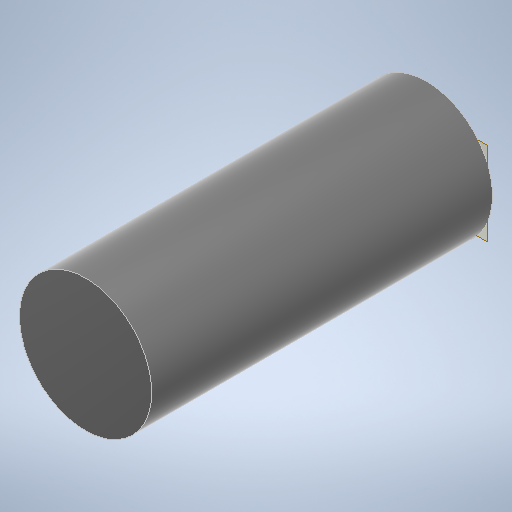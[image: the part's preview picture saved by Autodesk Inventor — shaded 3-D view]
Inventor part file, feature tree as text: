
AUTODESK INVENTOR PART (.ipt)
format: ipt  version: 2025.1 (Build 291241020, 241B)  size: 427,520 bytes
history: native  units: mm
features: extrude x8, sketch x8, plane x1, mirror x1
ambient origin geometry x8: Origin, YZ Plane, XZ Plane, XY Plane, X Axis, Y Axis, Z Axis, Center Point
bodies: Solid1 (feature_tree)
feature tree (18):
  extrude  "Extrusion1"  Depth=39.0mm
  plane  "Work Plane1"
  extrude  "Extrusion2"  Depth=3.0mm TaperAngle=0.0deg
  mirror  "Mirror1"
  extrude  "Extrusion5"  Depth=10.0mm TaperAngle=0.0deg
  extrude  "Extrusion6"  Depth=7.0mm
  extrude  "Extrusion7"  Depth=20.4mm
  extrude  "Extrusion8"  TaperAngle=0.0deg  [1 undecoded]
  extrude  "Extrusion9"  Depth=0.9mm
  extrude  "Extrusion10"  [1 undecoded]
  sketch  "Sketch1"  dims[d0=33.0mm d1=39.0mm]
  sketch  "Sketch2"  dims[d2=195.0mm d3=0.0mm d4=3.0mm d5=0.0mm]
  sketch  "Sketch5"  dims[d12=22.0mm d13=10.0mm d14=0.0mm]
  sketch  "Sketch6"  dims[d15=0.0mm d16=0.0mm d17=7.0mm]
  sketch  "Sketch7"  dims[d18=0.0mm d19=0.0mm d20=20.4mm]
  sketch  "Sketch8"  dims[d21=5.0mm d22=0.0mm d23=0.0mm d24=0.0mm]
  sketch  "Sketch9"  dims[d25=33.0mm d26=0.9mm]
  sketch  "Sketch10"  dims[d27=3.1mm d28=0.0mm]
note: 2 required parameter values undecoded (feature->parameter linkage not recoverable at this tier; creation-order binding heuristic only, values carry confidence <= 0.55)
